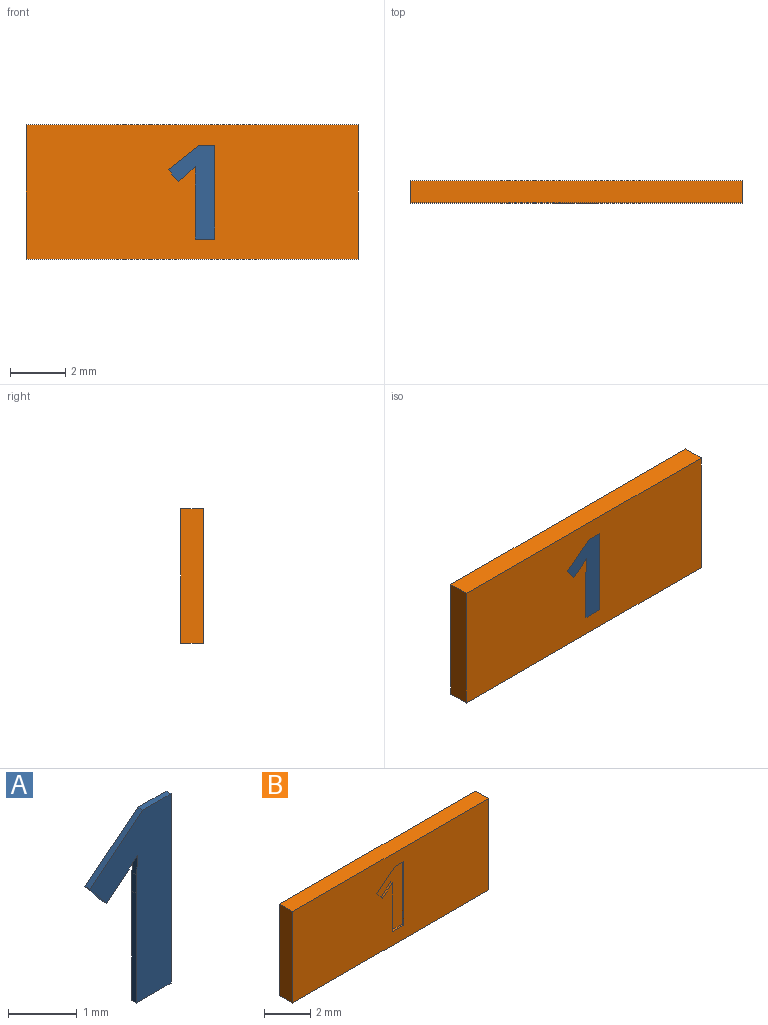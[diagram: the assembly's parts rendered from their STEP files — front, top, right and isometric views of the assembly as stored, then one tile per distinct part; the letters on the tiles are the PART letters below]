
ASSEMBLY  parts=2 mates=1
PART A: 12 faces, bbox 1.7x0.1x3.4 mm
  f0: plane 3.37x1.67mm, normal (0,-1,0), area 2.9mm2, adj f1,f2,f3,f4,f5,f6,f7,f9
  f1: plane 0.59x0.1mm, normal (0,0,1), area 0.1mm2, adj f0,f2,f8,f10
  f2: plane 1.09x0.86mm, normal (-0.62,0,0.78), area 0.1mm2, adj f0,f1,f3,f8
  f3: plane 0.43x0.34mm, normal (-0.78,0,-0.63), area 0.1mm2, adj f0,f2,f4,f8
  f4: plane 0.39x0.31mm, normal (0.63,0,-0.78), area 0mm2, adj f0,f3,f5,f8
  f5: extruded ~0.25x0.23mm, area 0mm2, adj f0,f4,f6,f8
  f6: plane 0.35x0.1mm, normal (-1,0,0.03), area 0mm2, adj f0,f5,f7,f8
  f7: plane 0.32x0.1mm, normal (-1,0,0.02), area 0mm2, adj f0,f6,f8,f9
  f8: plane 3.37x1.67mm, normal (0,1,0), area 2.9mm2, adj f1,f2,f3,f4,f5,f6,f7,f9
  f9: plane 1.95x0.1mm, normal (-1,0,0), area 0.2mm2, adj f0,f7,f8,f11
  f10: plane 3.37x0.1mm, normal (1,0,0), area 0.3mm2, adj f0,f1,f8,f11
  f11: plane 0.71x0.1mm, normal (0,0,-1), area 0.1mm2, adj f0,f8,f9,f10
PART B: 17 faces, bbox 12x0.8x4.9 mm
  f0: plane 12x4.85mm, normal (0,-1,0), area 55.3mm2, adj f1,f2,f3,f4,f6,f7,f8,f9
  f1: plane 4.85x0.8mm, normal (1,0,0), area 3.9mm2, adj f0,f2,f4,f5
  f2: plane 12x0.8mm, normal (0,0,1), area 9.6mm2, adj f0,f1,f3,f5
  f3: plane 4.85x0.8mm, normal (-1,0,0), area 3.9mm2, adj f0,f2,f4,f5
  f4: plane 12x0.8mm, normal (0,0,-1), area 9.6mm2, adj f0,f1,f3,f5
  f5: plane 12x4.85mm, normal (0,1,0), area 58.2mm2, adj f1,f2,f3,f4
  f6: plane 3.37x0.1mm, normal (-1,0,0), area 0.3mm2, adj f0,f7,f15,f16
  f7: plane 0.59x0.1mm, normal (0,0,-1), area 0.1mm2, adj f0,f6,f8,f16
  f8: plane 1.09x0.86mm, normal (0.62,0,-0.78), area 0.1mm2, adj f0,f7,f9,f16
  f9: plane 0.43x0.34mm, normal (0.78,0,0.63), area 0.1mm2, adj f0,f8,f10,f16
  f10: plane 0.39x0.31mm, normal (-0.63,0,0.78), area 0mm2, adj f0,f9,f11,f16
  f11: extruded ~0.25x0.23mm, area 0mm2, adj f0,f10,f12,f16
  f12: plane 0.35x0.1mm, normal (1,0,-0.03), area 0mm2, adj f0,f11,f13,f16
  f13: plane 0.32x0.1mm, normal (1,0,-0.02), area 0mm2, adj f0,f12,f14,f16
  f14: plane 1.95x0.1mm, normal (1,0,0), area 0.2mm2, adj f0,f13,f15,f16
  f15: plane 0.71x0.1mm, normal (0,0,1), area 0.1mm2, adj f0,f6,f14,f16
  f16: plane 3.37x1.67mm, normal (0,-1,0), area 2.9mm2, adj f6,f7,f8,f9,f10,f11,f12,f13
PLACE A t=(-1.56,0.4,0.01)mm
PLACE B t=(0.01,0.4,0.01)mm
MATE fastened A.f0 <-> B.f0  axis (0,-1,0) through (0.12,-0.4,-1.69)mm
